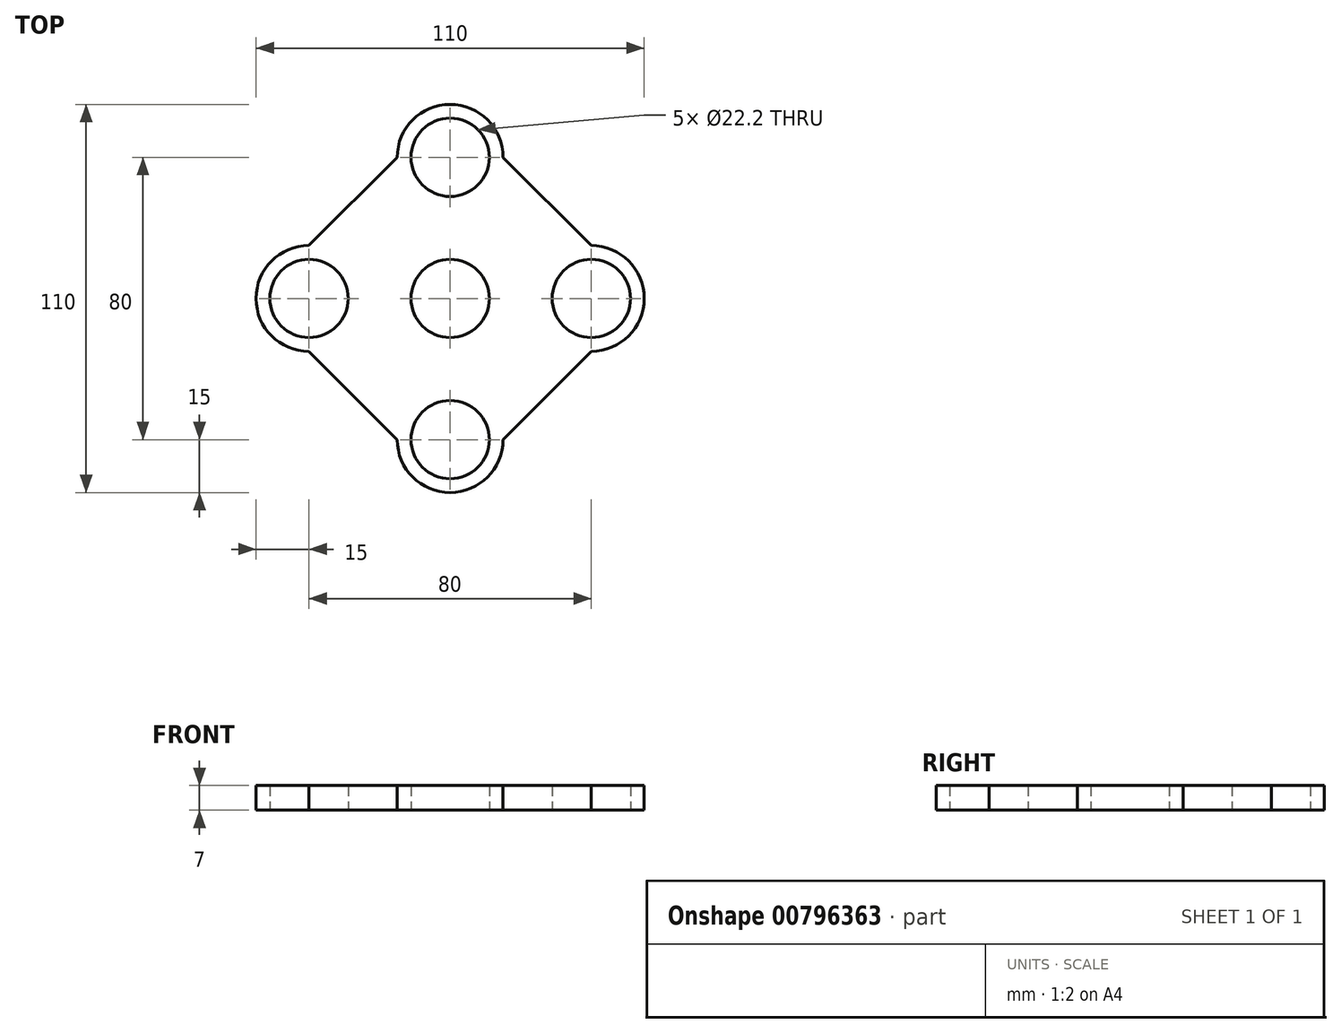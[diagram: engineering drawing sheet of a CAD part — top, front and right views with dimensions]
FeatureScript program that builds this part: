
annotation { "Feature Type Name" : "Feature", "Feature Type Description" : "" }
export const myFeature = defineFeature(function(context is Context, id is Id, definition is map)
    precondition{}
    {
        {
            var Q0;
            Q0=qCreatedBy(makeId("Top.planeOp"),FACE);
            var sketch = newSketch(context, id + "F0", { "sketchPlane" : qUnion([Q0])});
            skCircle(sketch, "E0", {"center": v(0, 0) * mm, "radius": 11.1 * mm});
            skCircle(sketch, "E1", {"center": v(0, 40) * mm, "radius": 11.1 * mm});
            skArc(sketch, "E2", {"start": v(15, 40) * mm, "mid": v(0, 55) * mm, "end": v(-15, 40) * mm});
            skCircle(sketch, "E3.1.0", {"center": v(40, 0) * mm, "radius": 11.1 * mm});
            skCircle(sketch, "E3.2.0", {"center": v(0, -40) * mm, "radius": 11.1 * mm});
            skCircle(sketch, "E3.3.0", {"center": v(-40, 0) * mm, "radius": 11.1 * mm});
            skLineSegment(sketch, "E3.anchor1", {"start": v(0, 0) * mm, "end": v(0, 40) * mm, "construction": true});
            skLineSegment(sketch, "E3.anchor2", {"start": v(0, 0) * mm, "end": v(-40, 0) * mm, "construction": true});
            skArc(sketch, "E4.1.0", {"start": v(-40, 15) * mm, "mid": v(-55, 0) * mm, "end": v(-40, -15) * mm});
            skArc(sketch, "E4.2.0", {"start": v(-15, -40) * mm, "mid": v(0, -55) * mm, "end": v(15, -40) * mm});
            skArc(sketch, "E4.3.0", {"start": v(40, -15) * mm, "mid": v(55, 0) * mm, "end": v(40, 15) * mm});
            skLineSegment(sketch, "E5", {"start": v(-40, 15) * mm, "end": v(-15, 40) * mm});
            skLineSegment(sketch, "E6", {"start": v(15, 40) * mm, "end": v(40, 15) * mm});
            skLineSegment(sketch, "E7", {"start": v(-40, -15) * mm, "end": v(-15, -40) * mm});
            skLineSegment(sketch, "E8", {"start": v(15, -40) * mm, "end": v(40, -15) * mm});
            skSolve(sketch);
        }
        {
            var Q0;
            Q0=makeQuery(id+"F0.imprint","IMPRINT",FACE,{"disambiguationData":[TD([[makeQuery(id+"F0.imprint","IMPRINT",EDGE,{"derivedFrom":sQuery(id+"F0.wireOp",EDGE,"E0")}),-1.0]])]});
            extrude(context, id + "F1", {"entities" : qUnion([Q0]), "endBound" : BoundingType.SYMMETRIC, "depth" : 7 * mm, "offsetDistance" : 25 * mm});
        }
    });
